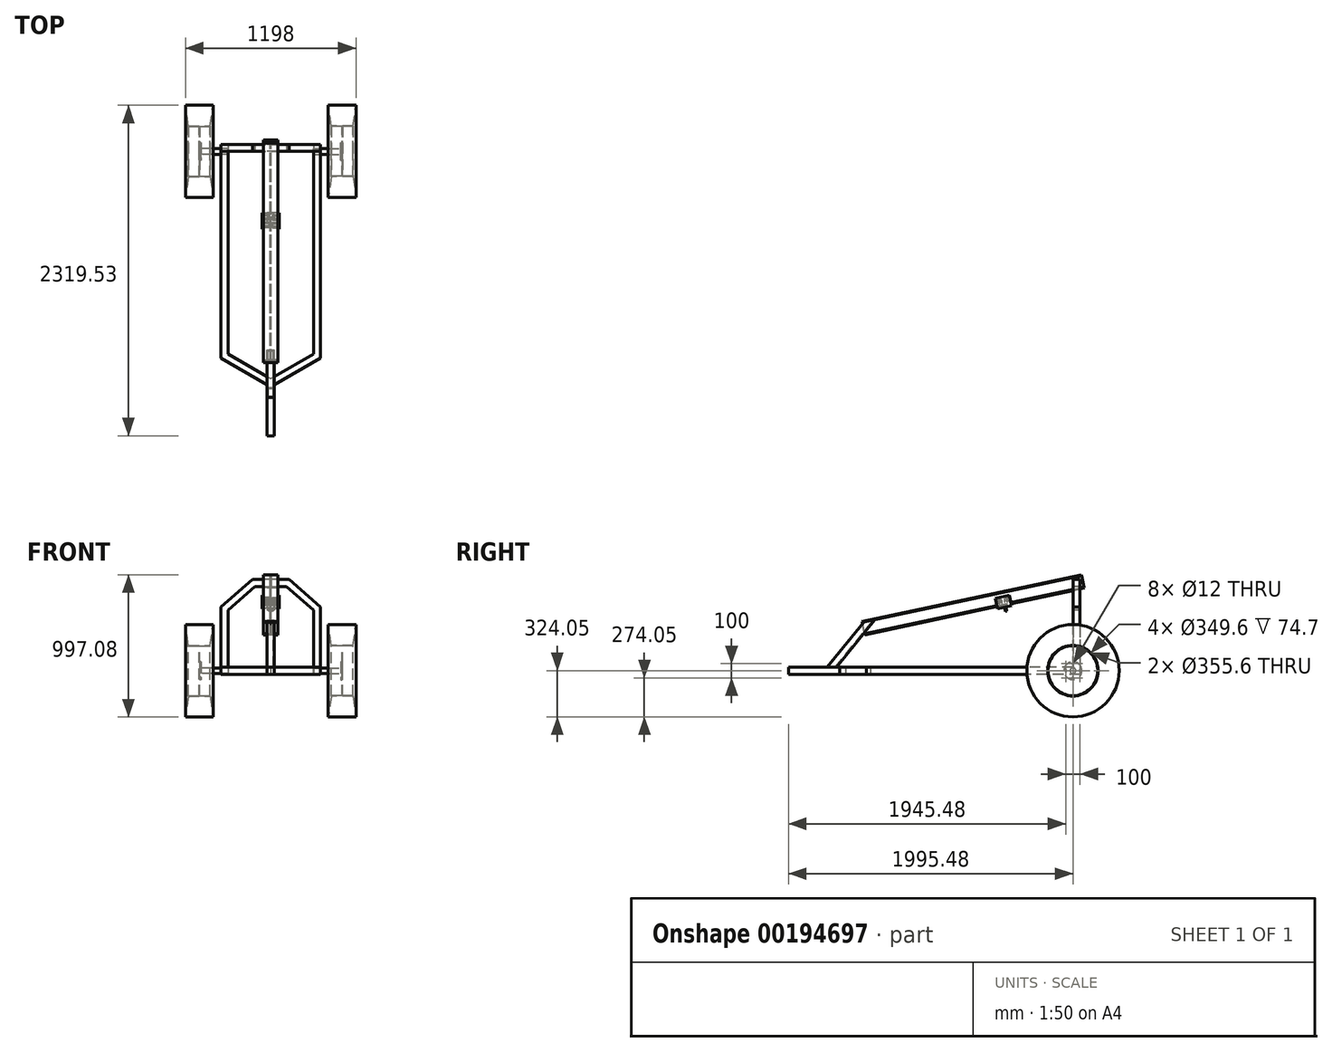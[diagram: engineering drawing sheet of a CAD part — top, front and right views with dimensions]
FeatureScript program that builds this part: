
annotation { "Feature Type Name" : "Feature", "Feature Type Description" : "" }
export const myFeature = defineFeature(function(context is Context, id is Id, definition is map)
    precondition{}
    {
        {
            assignVariable(context, id + "F0", {"name" : "Track", "anyValue" : 1000});
        }
        {
            assignVariable(context, id + "F1", {"name" : "AxelLength", "anyValue" : 200});
        }
        {
            var Q0;
            Q0=qCreatedBy(makeId("Right.planeOp"),FACE);
            cPlane(context, id + "F2", {"entities" : qUnion([Q0]), "cplaneType" : CPlaneType.OFFSET, "offset" : (getVariable(context, 'Track') / 2) * mm, "oppositeDirection" : true, "width" : 150 * mm, "height" : 150 * mm});
        }
        {
            var Q0;
            Q0=qCreatedBy(id+"F2.planeOp",FACE);
            var sketch = newSketch(context, id + "F3", { "sketchPlane" : qUnion([Q0])});
            skCircle(sketch, "E0", {"center": v(0, 0) * mm, "radius": 20 * mm});
            skSolve(sketch);
        }
        {
            var Q0;
            Q0 = qSketchRegion(id + "F3", true);
            extrude(context, id + "F4", {"entities" : qUnion([Q0]), "depth" : (getVariable(context, 'AxelLength')) * mm});
        }
        {
            var Q0;
            Q0=makeQuery(id+"F4.opExtrude","CAP_FACE",FACE,{"disambiguationData":[OSD([sQuery(id+"F3.wireOp",EDGE,"E0")])],"isStart":true});
            var sketch = newSketch(context, id + "F5", { "sketchPlane" : qUnion([Q0])});
            skCircle(sketch, "E1", {"center": v(0, 0) * mm, "radius": 62.5 * mm});
            skCircle(sketch, "E2", {"center": v(0, 50) * mm, "radius": 6 * mm});
            skCircle(sketch, "E3.1.0", {"center": v(-50, 0) * mm, "radius": 6 * mm});
            skCircle(sketch, "E3.2.0", {"center": v(0, -50) * mm, "radius": 6 * mm});
            skCircle(sketch, "E3.3.0", {"center": v(50, 0) * mm, "radius": 6 * mm});
            skSolve(sketch);
        }
        {
            var Q0;
            Q0 = qSketchRegion(id + "F5", true);
            extrude(context, id + "F6", {"entities" : qUnion([Q0]), "operationType" : NewBodyOperationType.ADD, "oppositeDirection" : true, "depth" : 10 * mm});
        }
        {
            var Q0;
            Q0=qCreatedBy(makeId("Front.planeOp"),FACE);
            var sketch = newSketch(context, id + "F7", { "sketchPlane" : qUnion([Q0])});
            skLineSegment(sketch, "E4", {"start": v(-500, 0) * mm, "end": v(-500, 174.8) * mm});
            skLineSegment(sketch, "E5", {"start": v(-500, 174.8) * mm, "end": v(-425.3, 174.8) * mm});
            skLineSegment(sketch, "E6", {"start": v(-425.3, 174.8) * mm, "end": v(-425.3, 177.8) * mm});
            skLineSegment(sketch, "E7", {"start": v(-425.3, 177.8) * mm, "end": v(-577.7, 177.8) * mm});
            skLineSegment(sketch, "E8", {"start": v(-577.7, 177.8) * mm, "end": v(-577.7, 174.8) * mm});
            skLineSegment(sketch, "E9", {"start": v(-577.7, 174.8) * mm, "end": v(-503, 174.8) * mm});
            skLineSegment(sketch, "E10", {"start": v(-503, 174.8) * mm, "end": v(-503, 0) * mm});
            skLineSegment(sketch, "E11", {"start": v(-503, 0) * mm, "end": v(-500, 0) * mm});
            skLineSegment(sketch, "E12", {"start": v(-501.5, 192.49) * mm, "end": v(-501.5, -36.04) * mm, "construction": true});
            skSolve(sketch);
        }
        {
            var Q0;
            Q0 = qSketchRegion(id + "F7", true);
            var Q1;
            Q1=makeQuery(id+"F4.opExtrude","SWEPT_FACE",FACE,{"disambiguationData":[OSD([sQuery(id+"F3.wireOp",EDGE,"E0")])]});
            revolve(context, id + "F8", {"entities" : qUnion([Q0]), "axis" : qUnion([Q1]), "revolveType" : RevolveType.FULL});
        }
        {
            var Q0;
            Q0=qCreatedBy(makeId("Front.planeOp"),FACE);
            var sketch = newSketch(context, id + "F9", { "sketchPlane" : qUnion([Q0])});
            skLineSegment(sketch, "E13", {"start": v(-425.3, 177.8) * mm, "end": v(-404, 324.05) * mm});
            skLineSegment(sketch, "E14", {"start": v(-404, 324.05) * mm, "end": v(-599, 324.05) * mm});
            skLineSegment(sketch, "E15", {"start": v(-599, 324.05) * mm, "end": v(-577.7, 177.8) * mm});
            skLineSegment(sketch, "E16", {"start": v(-577.7, 177.8) * mm, "end": v(-425.3, 177.8) * mm});
            skLineSegment(sketch, "E17.0", {"start": v(-425.3, 177.8) * mm, "end": v(-425.3, -177.8) * mm, "construction": true});
            skLineSegment(sketch, "E18.0", {"start": v(-577.7, 177.8) * mm, "end": v(-577.7, -177.8) * mm, "construction": true});
            skLineSegment(sketch, "E19", {"start": v(-501.5, 369.37) * mm, "end": v(-501.5, 43.75) * mm, "construction": true});
            skSolve(sketch);
        }
        {
            var Q0;
            Q0 = qSketchRegion(id + "F9", true);
            var Q1;
            Q1=makeQuery(id+"F4.opExtrude","SWEPT_FACE",FACE,{"disambiguationData":[OSD([sQuery(id+"F3.wireOp",EDGE,"E0")])]});
            revolve(context, id + "F10", {"entities" : qUnion([Q0]), "axis" : qUnion([Q1]), "revolveType" : RevolveType.FULL});
        }
        {
            var Q0;
            Q0=makeQuery(id+"F4.opExtrude","SWEPT_BODY",BODY,{"disambiguationData":[OSD([sQuery(id+"F3.wireOp",EDGE,"E0")])]});
            var Q1;
            Q1=makeQuery(id+"F8.opRevolve","SWEPT_BODY",BODY,{"disambiguationData":[OSD([sQuery(id+"F7.wireOp",EDGE,"E4"),sQuery(id+"F7.wireOp",EDGE,"E5"),sQuery(id+"F7.wireOp",EDGE,"E6"),sQuery(id+"F7.wireOp",EDGE,"E7"),sQuery(id+"F7.wireOp",EDGE,"E8"),sQuery(id+"F7.wireOp",EDGE,"E9"),sQuery(id+"F7.wireOp",EDGE,"E10"),sQuery(id+"F7.wireOp",EDGE,"E11")])]});
            var Q2;
            Q2=makeQuery(id+"F10.opRevolve","SWEPT_BODY",BODY,{"disambiguationData":[OSD([sQuery(id+"F9.wireOp",EDGE,"E13"),sQuery(id+"F9.wireOp",EDGE,"E14"),sQuery(id+"F9.wireOp",EDGE,"E15"),sQuery(id+"F9.wireOp",EDGE,"E16")])]});
            var Q3;
            Q3=qCreatedBy(makeId("Right.planeOp"),FACE);
            mirror(context, id + "F11", {"entities" : qUnion([Q0, Q1, Q2]), "mirrorPlane" : qUnion([Q3])});
        }
        {
            var Q0;
            Q0=qCreatedBy(makeId("Top.planeOp"),FACE);
            var sketch = newSketch(context, id + "F12", { "sketchPlane" : qUnion([Q0])});
            skLineSegment(sketch, "E20.bottom", {"start": v(-350, 50) * mm, "end": v(-300, 50) * mm});
            skLineSegment(sketch, "E20.top", {"start": v(-350, -1450) * mm, "end": v(-300, -1421.13) * mm});
            skLineSegment(sketch, "E20.left", {"start": v(-350, 50) * mm, "end": v(-350, -1450) * mm});
            skLineSegment(sketch, "E20.right", {"start": v(-300, 50) * mm, "end": v(-300, -1421.13) * mm});
            skLineSegment(sketch, "E21.bottom", {"start": v(300, 50) * mm, "end": v(350, 50) * mm});
            skLineSegment(sketch, "E21.top", {"start": v(300, -1421.13) * mm, "end": v(350, -1450) * mm});
            skLineSegment(sketch, "E21.left", {"start": v(300, 50) * mm, "end": v(300, -1421.13) * mm});
            skLineSegment(sketch, "E21.right", {"start": v(350, 50) * mm, "end": v(350, -1450) * mm});
            skLineSegment(sketch, "E22", {"start": v(0, 405.97) * mm, "end": v(0, -2997.8) * mm, "construction": true});
            skLineSegment(sketch, "E23", {"start": v(-300, -1421.13) * mm, "end": v(0, -1594.34) * mm});
            skLineSegment(sketch, "E24", {"start": v(0, -1594.34) * mm, "end": v(300, -1421.13) * mm});
            skLineSegment(sketch, "E25", {"start": v(350, -1450) * mm, "end": v(0, -1652.07) * mm});
            skLineSegment(sketch, "E26", {"start": v(0, -1652.07) * mm, "end": v(-350, -1450) * mm});
            skLineSegment(sketch, "E27.bottom", {"start": v(-25, -1637.64) * mm, "end": v(25, -1637.64) * mm});
            skLineSegment(sketch, "E27.top", {"start": v(-25, -1995.48) * mm, "end": v(25, -1995.48) * mm});
            skLineSegment(sketch, "E27.left", {"start": v(-25, -1637.64) * mm, "end": v(-25, -1995.48) * mm});
            skLineSegment(sketch, "E27.right", {"start": v(25, -1637.64) * mm, "end": v(25, -1995.48) * mm});
            skSolve(sketch);
        }
        {
            var Q0;
            Q0 = qSketchRegion(id + "F12", true);
            extrude(context, id + "F13", {"entities" : qUnion([Q0]), "endBound" : BoundingType.SYMMETRIC, "depth" : 50 * mm});
        }
        {
            var Q0;
            Q0=qCreatedBy(makeId("Front.planeOp"),FACE);
            var sketch = newSketch(context, id + "F14", { "sketchPlane" : qUnion([Q0])});
            skLineSegment(sketch, "E28", {"start": v(350, 25) * mm, "end": v(350, 447.68) * mm});
            skLineSegment(sketch, "E29", {"start": v(350, 447.68) * mm, "end": v(129.1, 641.07) * mm});
            skLineSegment(sketch, "E30", {"start": v(129.1, 641.07) * mm, "end": v(-129.1, 641.07) * mm});
            skLineSegment(sketch, "E31", {"start": v(-129.1, 641.07) * mm, "end": v(-350, 447.68) * mm});
            skLineSegment(sketch, "E32", {"start": v(-350, 447.68) * mm, "end": v(-350, 25) * mm});
            skLineSegment(sketch, "E33", {"start": v(-350, 25) * mm, "end": v(-300, 25) * mm});
            skLineSegment(sketch, "E34", {"start": v(-300, 25) * mm, "end": v(-300, 425) * mm});
            skLineSegment(sketch, "E35", {"start": v(-300, 425) * mm, "end": v(-110.3, 591.07) * mm});
            skLineSegment(sketch, "E36", {"start": v(-110.3, 591.07) * mm, "end": v(110.3, 591.07) * mm});
            skLineSegment(sketch, "E37", {"start": v(110.3, 591.07) * mm, "end": v(300, 425) * mm});
            skLineSegment(sketch, "E38", {"start": v(300, 425) * mm, "end": v(300, 25) * mm});
            skLineSegment(sketch, "E39", {"start": v(300, 25) * mm, "end": v(350, 25) * mm});
            skLineSegment(sketch, "E40", {"start": v(0, 637.9) * mm, "end": v(0, -203.17) * mm, "construction": true});
            skSolve(sketch);
        }
        {
            var Q0;
            Q0 = qSketchRegion(id + "F14", true);
            extrude(context, id + "F15", {"entities" : qUnion([Q0]), "operationType" : NewBodyOperationType.ADD, "oppositeDirection" : true, "depth" : 50 * mm});
        }
        {
            var Q0;
            Q0=makeQuery(id+"F15.opExtrude","CAP_EDGE",EDGE,{"disambiguationData":[OSD([sQuery(id+"F14.wireOp",EDGE,"E36")])],"isStart":true});
            cPlane(context, id + "F16", {"entities" : qUnion([Q0]), "cplaneType" : CPlaneType.LINE_ANGLE, "offset" : 25 * mm, "angle" : 12 * degree, "width" : 150 * mm, "height" : 150 * mm});
        }
        {
            var Q0;
            Q0=qCreatedBy(id+"F16.planeOp",FACE);
            var sketch = newSketch(context, id + "F17", { "sketchPlane" : qUnion([Q0])});
            skLineSegment(sketch, "E41", {"start": v(50, 646) * mm, "end": v(-50, 646) * mm});
            skLineSegment(sketch, "E42", {"start": v(-50, 646) * mm, "end": v(-50, 638) * mm});
            skLineSegment(sketch, "E43", {"start": v(-50, 638) * mm, "end": v(-2.5, 638) * mm});
            skLineSegment(sketch, "E44", {"start": v(-2.5, 638) * mm, "end": v(-2.5, 558) * mm});
            skLineSegment(sketch, "E45", {"start": v(-2.5, 558) * mm, "end": v(-50, 558) * mm});
            skLineSegment(sketch, "E46", {"start": v(-50, 558) * mm, "end": v(-50, 550) * mm});
            skLineSegment(sketch, "E47", {"start": v(-50, 550) * mm, "end": v(50, 550) * mm});
            skLineSegment(sketch, "E48", {"start": v(50, 550) * mm, "end": v(50, 558) * mm});
            skLineSegment(sketch, "E49", {"start": v(50, 558) * mm, "end": v(2.5, 558) * mm});
            skLineSegment(sketch, "E50", {"start": v(2.5, 558) * mm, "end": v(2.5, 638) * mm});
            skLineSegment(sketch, "E51", {"start": v(2.5, 638) * mm, "end": v(50, 638) * mm});
            skLineSegment(sketch, "E52", {"start": v(50, 638) * mm, "end": v(50, 646) * mm});
            skLineSegment(sketch, "E53", {"start": v(0, 0) * mm, "end": v(0, 1079.78) * mm, "construction": true});
            skSolve(sketch);
        }
        {
            var Q0;
            Q0 = qSketchRegion(id + "F17", true);
            extrude(context, id + "F18", {"entities" : qUnion([Q0]), "oppositeDirection" : true, "depth" : 1500 * mm, "hasSecondDirection" : true, "secondDirectionOppositeDirection" : false, "secondDirectionDepth" : 75 * mm});
        }
        {
            var Q0;
            Q0=makeQuery(id+"F13.opExtrude","CAP_FACE",FACE,{"disambiguationData":[OSD([sQuery(id+"F12.wireOp",EDGE,"E20.bottom"),sQuery(id+"F12.wireOp",EDGE,"E20.left"),sQuery(id+"F12.wireOp",EDGE,"E20.right"),sQuery(id+"F12.wireOp",EDGE,"E21.bottom"),sQuery(id+"F12.wireOp",EDGE,"E21.left"),sQuery(id+"F12.wireOp",EDGE,"E21.right"),sQuery(id+"F12.wireOp",EDGE,"E23"),sQuery(id+"F12.wireOp",EDGE,"E24"),sQuery(id+"F12.wireOp",EDGE,"E25"),sQuery(id+"F12.wireOp",EDGE,"E26"),sQuery(id+"F12.wireOp",EDGE,"E27.top"),sQuery(id+"F12.wireOp",EDGE,"E27.left"),sQuery(id+"F12.wireOp",EDGE,"E27.right")])],"isStart":false});
            var Q1;
            Q1=makeQuery(id+"F18.opExtrude","CAP_FACE",FACE,{"disambiguationData":[OSD([sQuery(id+"F17.wireOp",EDGE,"E41"),sQuery(id+"F17.wireOp",EDGE,"E42"),sQuery(id+"F17.wireOp",EDGE,"E43"),sQuery(id+"F17.wireOp",EDGE,"E44"),sQuery(id+"F17.wireOp",EDGE,"E45"),sQuery(id+"F17.wireOp",EDGE,"E46"),sQuery(id+"F17.wireOp",EDGE,"E47"),sQuery(id+"F17.wireOp",EDGE,"E48"),sQuery(id+"F17.wireOp",EDGE,"E49"),sQuery(id+"F17.wireOp",EDGE,"E50"),sQuery(id+"F17.wireOp",EDGE,"E51"),sQuery(id+"F17.wireOp",EDGE,"E52")])],"isStart":false});
            cPlane(context, id + "F19", {"entities" : qUnion([Q0, Q1]), "cplaneType" : CPlaneType.MID_PLANE, "offset" : 25 * mm, "width" : 150 * mm, "height" : 150 * mm});
        }
        {
            var Q0;
            Q0=qCreatedBy(id+"F19.planeOp",FACE);
            var sketch = newSketch(context, id + "F20", { "sketchPlane" : qUnion([Q0])});
            skLineSegment(sketch, "E54.bottom", {"start": v(-25, -1356.38) * mm, "end": v(25, -1356.38) * mm});
            skLineSegment(sketch, "E54.top", {"start": v(-25, -1306.38) * mm, "end": v(25, -1306.38) * mm});
            skLineSegment(sketch, "E54.left", {"start": v(-25, -1356.38) * mm, "end": v(-25, -1306.38) * mm});
            skLineSegment(sketch, "E54.right", {"start": v(25, -1356.38) * mm, "end": v(25, -1306.38) * mm});
            skLineSegment(sketch, "E55", {"start": v(0, -1419.07) * mm, "end": v(0, -1239.41) * mm, "construction": true});
            skLineSegment(sketch, "E56", {"start": v(-112.4, -1331.38) * mm, "end": v(129.21, -1331.38) * mm, "construction": true});
            skLineSegment(sketch, "E57.0", {"start": v(-20, -1351.38) * mm, "end": v(20, -1351.38) * mm});
            skLineSegment(sketch, "E57.1", {"start": v(-20, -1351.38) * mm, "end": v(-20, -1311.38) * mm});
            skLineSegment(sketch, "E57.2", {"start": v(-20, -1311.38) * mm, "end": v(20, -1311.38) * mm});
            skLineSegment(sketch, "E57.3", {"start": v(20, -1351.38) * mm, "end": v(20, -1311.38) * mm});
            skSolve(sketch);
        }
        {
            var Q0;
            Q0 = qSketchRegion(id + "F20", true);
            var Q1;
            Q1=makeQuery(id+"F13.opExtrude","SWEPT_BODY",BODY,{"disambiguationData":[OSD([sQuery(id+"F12.wireOp",EDGE,"E20.bottom"),sQuery(id+"F12.wireOp",EDGE,"E20.left"),sQuery(id+"F12.wireOp",EDGE,"E20.right"),sQuery(id+"F12.wireOp",EDGE,"E21.bottom"),sQuery(id+"F12.wireOp",EDGE,"E21.left"),sQuery(id+"F12.wireOp",EDGE,"E21.right"),sQuery(id+"F12.wireOp",EDGE,"E23"),sQuery(id+"F12.wireOp",EDGE,"E24"),sQuery(id+"F12.wireOp",EDGE,"E25"),sQuery(id+"F12.wireOp",EDGE,"E26"),sQuery(id+"F12.wireOp",EDGE,"E27.top"),sQuery(id+"F12.wireOp",EDGE,"E27.left"),sQuery(id+"F12.wireOp",EDGE,"E27.right")])]});
            var Q2;
            Q2=makeQuery(id+"F18.opExtrude","SWEPT_BODY",BODY,{"disambiguationData":[OSD([sQuery(id+"F17.wireOp",EDGE,"E41"),sQuery(id+"F17.wireOp",EDGE,"E42"),sQuery(id+"F17.wireOp",EDGE,"E43"),sQuery(id+"F17.wireOp",EDGE,"E44"),sQuery(id+"F17.wireOp",EDGE,"E45"),sQuery(id+"F17.wireOp",EDGE,"E46"),sQuery(id+"F17.wireOp",EDGE,"E47"),sQuery(id+"F17.wireOp",EDGE,"E48"),sQuery(id+"F17.wireOp",EDGE,"E49"),sQuery(id+"F17.wireOp",EDGE,"E50"),sQuery(id+"F17.wireOp",EDGE,"E51"),sQuery(id+"F17.wireOp",EDGE,"E52")])]});
            extrude(context, id + "F21", {"entities" : qUnion([Q0]), "endBound" : BoundingType.UP_TO_BODY, "oppositeDirection" : true, "endBoundEntityBody" : qUnion([Q1]), "depth" : 25 * mm, "hasSecondDirection" : true, "secondDirectionBound" : SecondDirectionBoundingType.UP_TO_BODY, "secondDirectionOppositeDirection" : false, "secondDirectionBoundEntityBody" : qUnion([Q2]), "secondDirectionDepth" : 25 * mm});
        }
        {
            var Q0;
            Q0=qCreatedBy(id+"F16.planeOp",FACE);
            cPlane(context, id + "F22", {"entities" : qUnion([Q0]), "cplaneType" : CPlaneType.OFFSET, "offset" : 500 * mm, "oppositeDirection" : true, "width" : 150 * mm, "height" : 150 * mm});
        }
        {
            var Q0;
            Q0=qCreatedBy(id+"F22.planeOp",FACE);
            var sketch = newSketch(context, id + "F23", { "sketchPlane" : qUnion([Q0])});
            skLineSegment(sketch, "E58", {"start": v(55.57, 610) * mm, "end": v(55.57, 540) * mm});
            skLineSegment(sketch, "E59", {"start": v(55.57, 540) * mm, "end": v(-55.57, 540) * mm});
            skLineSegment(sketch, "E60", {"start": v(-55.57, 540) * mm, "end": v(-55.57, 610) * mm});
            skLineSegment(sketch, "E61", {"start": v(-55.57, 610) * mm, "end": v(-60.57, 610) * mm});
            skLineSegment(sketch, "E62", {"start": v(-60.57, 610) * mm, "end": v(-60.57, 535) * mm});
            skLineSegment(sketch, "E63", {"start": v(-60.57, 535) * mm, "end": v(60.57, 535) * mm});
            skLineSegment(sketch, "E64", {"start": v(60.57, 535) * mm, "end": v(60.57, 610) * mm});
            skLineSegment(sketch, "E65", {"start": v(60.57, 610) * mm, "end": v(55.57, 610) * mm});
            skLineSegment(sketch, "E66", {"start": v(0, 482.07) * mm, "end": v(0, 689.61) * mm, "construction": true});
            skSolve(sketch);
        }
        {
            var Q0;
            Q0 = qSketchRegion(id + "F23", true);
            extrude(context, id + "F24", {"entities" : qUnion([Q0]), "endBound" : BoundingType.SYMMETRIC, "depth" : 100 * mm});
        }
        {
            var Q0;
            Q0=makeQuery(id+"F24.opExtrude","SWEPT_FACE",FACE,{"disambiguationData":[OSD([sQuery(id+"F23.wireOp",EDGE,"E64")])]});
            var sketch = newSketch(context, id + "F25", { "sketchPlane" : qUnion([Q0])});
            skLineSegment(sketch, "E67.0", {"start": v(1463.03, 259.49) * mm, "end": v(-77.55, 586.95) * mm, "construction": true});
            skCircle(sketch, "E68", {"center": v(516.02, 481.23) * mm, "radius": 20 * mm, "construction": true});
            skCircle(sketch, "E69", {"center": v(462.07, 492.7) * mm, "radius": 20 * mm, "construction": true});
            skLineSegment(sketch, "E70", {"start": v(513.31, 601.15) * mm, "end": v(467.91, 387.56) * mm, "construction": true});
            skCircle(sketch, "E71", {"center": v(462.07, 492.7) * mm, "radius": 7.5 * mm});
            skCircle(sketch, "E72", {"center": v(516.02, 481.23) * mm, "radius": 7.5 * mm});
            skSolve(sketch);
        }
        {
            var Q0;
            Q0 = qSketchRegion(id + "F25", true);
            extrude(context, id + "F26", {"entities" : qUnion([Q0]), "oppositeDirection" : true, "depth" : 50 * mm});
        }
        {
            var Q0;
            Q0=makeQuery(id+"F26.opExtrude","SWEPT_BODY",BODY,{"disambiguationData":[OSD([sQuery(id+"F25.wireOp",EDGE,"E72")])]});
            var Q1;
            Q1=makeQuery(id+"F26.opExtrude","SWEPT_BODY",BODY,{"disambiguationData":[OSD([sQuery(id+"F25.wireOp",EDGE,"E71")])]});
            var Q2;
            Q2=qCreatedBy(makeId("Right.planeOp"),FACE);
            mirror(context, id + "F27", {"operationType" : NewBodyOperationType.ADD, "entities" : qUnion([Q0, Q1]), "mirrorPlane" : qUnion([Q2])});
        }
        {
            var Q0;
            Q0=makeQuery(id+"F24.opExtrude","SWEPT_FACE",FACE,{"disambiguationData":[OSD([sQuery(id+"F23.wireOp",EDGE,"E58")])]});
            cPlane(context, id + "F28", {"entities" : qUnion([Q0]), "cplaneType" : CPlaneType.OFFSET, "offset" : 25 * mm, "width" : 150 * mm, "height" : 150 * mm});
        }
        {
            var Q0;
            Q0=qCreatedBy(id+"F28.planeOp",FACE);
            var sketch = newSketch(context, id + "F29", { "sketchPlane" : qUnion([Q0])});
            skLineSegment(sketch, "E73.0", {"start": v(-1463.03, 259.49) * mm, "end": v(77.55, 586.95) * mm, "construction": true});
            skCircle(sketch, "E74.0", {"center": v(-516.02, 481.23) * mm, "radius": 7.5 * mm, "construction": true});
            skCircle(sketch, "E75.0", {"center": v(-462.07, 492.7) * mm, "radius": 7.5 * mm, "construction": true});
            skCircle(sketch, "E76", {"center": v(-462.07, 492.7) * mm, "radius": 20 * mm});
            skCircle(sketch, "E77", {"center": v(-516.02, 481.23) * mm, "radius": 20 * mm});
            skSolve(sketch);
        }
        {
            var Q0;
            Q0 = qSketchRegion(id + "F29", true);
            extrude(context, id + "F30", {"entities" : qUnion([Q0]), "endBound" : BoundingType.SYMMETRIC, "depth" : 40 * mm});
        }
        {
            var Q0;
            Q0=makeQuery(id+"F30.opExtrude","SWEPT_BODY",BODY,{"disambiguationData":[OSD([sQuery(id+"F29.wireOp",EDGE,"E77")])]});
            var Q1;
            Q1=makeQuery(id+"F30.opExtrude","SWEPT_BODY",BODY,{"disambiguationData":[OSD([sQuery(id+"F29.wireOp",EDGE,"E76")])]});
            var Q2;
            Q2=qCreatedBy(makeId("Right.planeOp"),FACE);
            mirror(context, id + "F31", {"entities" : qUnion([Q0, Q1]), "mirrorPlane" : qUnion([Q2])});
        }
        {
            var Q0;
            Q0=qCreatedBy(id+"F22.planeOp",FACE);
            var sketch = newSketch(context, id + "F32", { "sketchPlane" : qUnion([Q0])});
            skLineSegment(sketch, "E78", {"start": v(0, 456.19) * mm, "end": v(0, 570.75) * mm, "construction": true});
            skLineSegment(sketch, "E79.0", {"start": v(-60.57, 535) * mm, "end": v(60.57, 535) * mm, "construction": true});
            skArc(sketch, "E80", {"start": v(20, 535) * mm, "mid": v(0, 515) * mm, "end": v(-20, 535) * mm});
            skArc(sketch, "E81", {"start": v(30, 535) * mm, "mid": v(0, 505) * mm, "end": v(-30, 535) * mm});
            skLineSegment(sketch, "E82", {"start": v(30, 535) * mm, "end": v(20, 535) * mm});
            skLineSegment(sketch, "E83", {"start": v(-20, 535) * mm, "end": v(-30, 535) * mm});
            skSolve(sketch);
        }
        {
            var Q0;
            Q0 = qSketchRegion(id + "F32", true);
            extrude(context, id + "F33", {"entities" : qUnion([Q0]), "operationType" : NewBodyOperationType.ADD, "depth" : 10 * mm});
        }
    });
